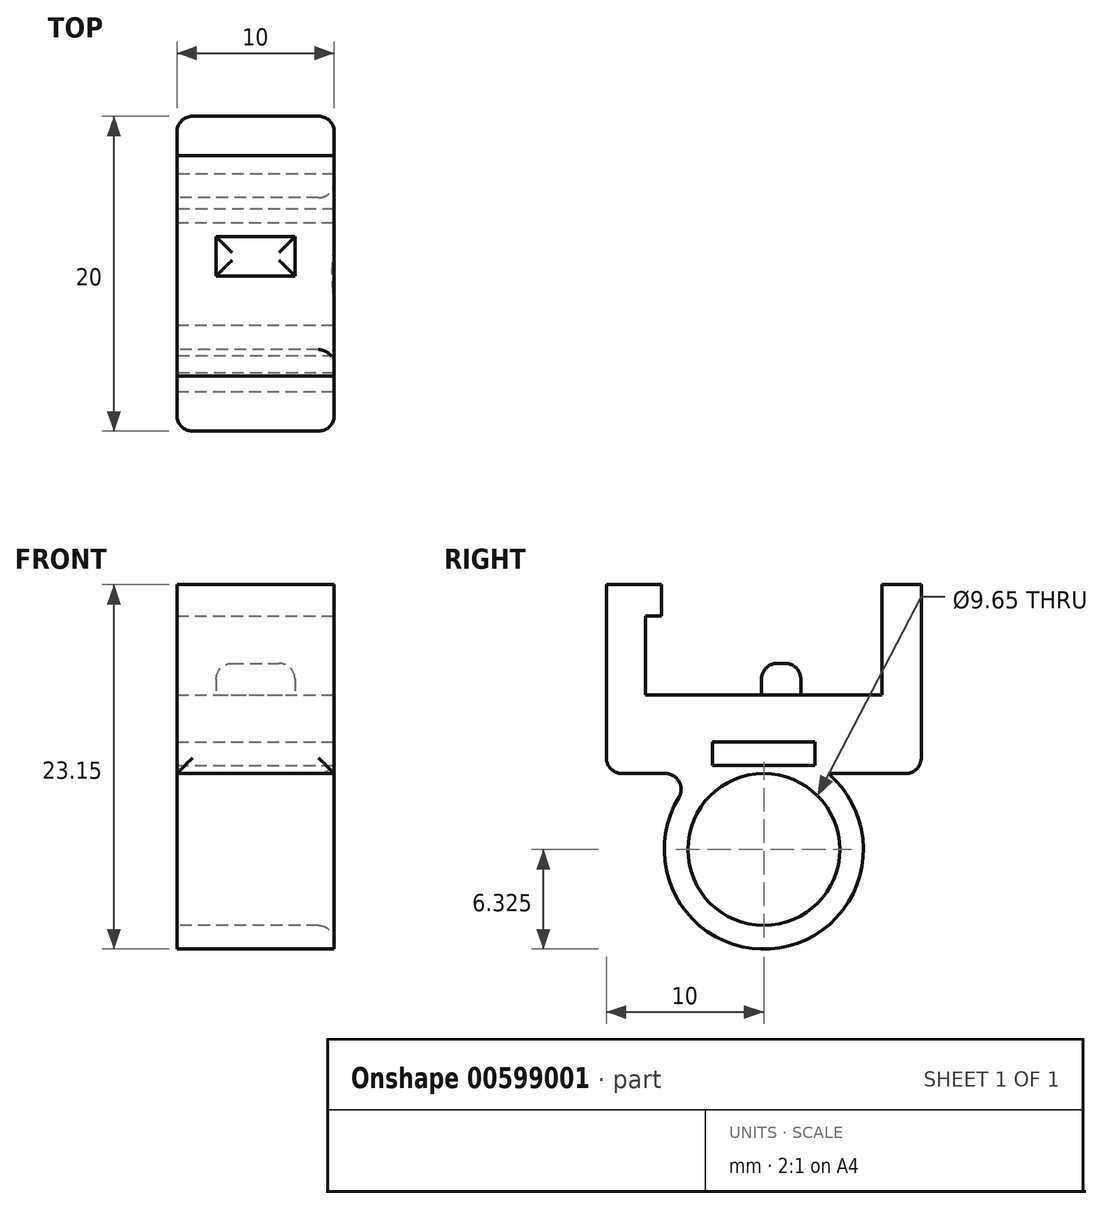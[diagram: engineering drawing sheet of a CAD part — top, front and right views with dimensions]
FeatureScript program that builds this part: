
annotation { "Feature Type Name" : "Feature", "Feature Type Description" : "" }
export const myFeature = defineFeature(function(context is Context, id is Id, definition is map)
    precondition{}
    {
        {
            var Q0;
            Q0=qCreatedBy(makeId("Top.planeOp"),FACE);
            var sketch = newSketch(context, id + "F0", { "sketchPlane" : qUnion([Q0])});
            skLineSegment(sketch, "E0.bottom", {"start": v(5, -10) * mm, "end": v(-5, -10) * mm});
            skLineSegment(sketch, "E0.top", {"start": v(5, 10) * mm, "end": v(-5, 10) * mm});
            skLineSegment(sketch, "E0.left", {"start": v(5, -10) * mm, "end": v(5, 10) * mm});
            skLineSegment(sketch, "E0.right", {"start": v(-5, -10) * mm, "end": v(-5, 10) * mm});
            skPoint(sketch, "E0.middle", {"position": v(0, 0) * mm});
            skSolve(sketch);
        }
        {
            var Q0;
            Q0 = qSketchRegion(id + "F0", true);
            extrude(context, id + "F1", {"entities" : qUnion([Q0]), "depth" : 5 * mm, "offsetDistance" : 25 * mm});
        }
        {
            var Q0;
            Q0=makeQuery(id+"F1.opExtrude","CAP_FACE",FACE,{"disambiguationData":[OSD([sQuery(id+"F0.wireOp",EDGE,"E0.bottom"),sQuery(id+"F0.wireOp",EDGE,"E0.top"),sQuery(id+"F0.wireOp",EDGE,"E0.left"),sQuery(id+"F0.wireOp",EDGE,"E0.right")])],"isStart":false});
            var sketch = newSketch(context, id + "F2", { "sketchPlane" : qUnion([Q0])});
            skLineSegment(sketch, "E1.bottom", {"start": v(-5, -7.5) * mm, "end": v(5, -7.5) * mm});
            skLineSegment(sketch, "E1.top", {"start": v(-5, -10) * mm, "end": v(5, -10) * mm});
            skLineSegment(sketch, "E1.left", {"start": v(-5, -7.5) * mm, "end": v(-5, -10) * mm});
            skLineSegment(sketch, "E1.right", {"start": v(5, -7.5) * mm, "end": v(5, -10) * mm});
            skLineSegment(sketch, "E2.MirrorCS", {"start": v(-5, 7.5) * mm, "end": v(5, 7.5) * mm});
            skLineSegment(sketch, "E3.MirrorCS", {"start": v(-5, 7.5) * mm, "end": v(-5, 10) * mm});
            skLineSegment(sketch, "E4.MirrorCS", {"start": v(-5, 10) * mm, "end": v(5, 10) * mm});
            skLineSegment(sketch, "E5.MirrorCS", {"start": v(5, 7.5) * mm, "end": v(5, 10) * mm});
            skSolve(sketch);
        }
        {
            var Q0;
            Q0 = qSketchRegion(id + "F2", true);
            extrude(context, id + "F3", {"entities" : qUnion([Q0]), "operationType" : NewBodyOperationType.ADD, "depth" : 7 * mm, "offsetDistance" : 25 * mm});
        }
        {
            var Q0;
            Q0=makeQuery(id+"F3.opExtrude","SWEPT_FACE",FACE,{"disambiguationData":[OSD([sQuery(id+"F2.wireOp",EDGE,"E1.bottom")])]});
            var sketch = newSketch(context, id + "F4", { "sketchPlane" : qUnion([Q0])});
            skLineSegment(sketch, "E6.bottom", {"start": v(5, 12) * mm, "end": v(-5, 12) * mm});
            skLineSegment(sketch, "E6.top", {"start": v(5, 10) * mm, "end": v(-5, 10) * mm});
            skLineSegment(sketch, "E6.left", {"start": v(5, 12) * mm, "end": v(5, 10) * mm});
            skLineSegment(sketch, "E6.right", {"start": v(-5, 12) * mm, "end": v(-5, 10) * mm});
            skSolve(sketch);
        }
        {
            var Q0;
            Q0 = qSketchRegion(id + "F4", true);
            extrude(context, id + "F5", {"entities" : qUnion([Q0]), "operationType" : NewBodyOperationType.ADD, "depth" : 1 * mm, "offsetDistance" : 25 * mm});
        }
        {
            var Q0;
            Q0=makeQuery(id+"F1.opExtrude","CAP_FACE",FACE,{"disambiguationData":[OSD([sQuery(id+"F0.wireOp",EDGE,"E0.bottom"),sQuery(id+"F0.wireOp",EDGE,"E0.top"),sQuery(id+"F0.wireOp",EDGE,"E0.left"),sQuery(id+"F0.wireOp",EDGE,"E0.right")])],"isStart":false});
            var sketch = newSketch(context, id + "F6", { "sketchPlane" : qUnion([Q0])});
            skLineSegment(sketch, "E7.bottom", {"start": v(-2.5, 2.35) * mm, "end": v(2.5, 2.35) * mm});
            skLineSegment(sketch, "E7.top", {"start": v(-2.5, -0.15) * mm, "end": v(2.5, -0.15) * mm});
            skLineSegment(sketch, "E7.left", {"start": v(-2.5, 2.35) * mm, "end": v(-2.5, -0.15) * mm});
            skLineSegment(sketch, "E7.right", {"start": v(2.5, 2.35) * mm, "end": v(2.5, -0.15) * mm});
            skSolve(sketch);
        }
        {
            var Q0;
            Q0 = qSketchRegion(id + "F6", true);
            extrude(context, id + "F7", {"entities" : qUnion([Q0]), "operationType" : NewBodyOperationType.ADD, "depth" : 2 * mm, "offsetDistance" : 25 * mm});
        }
        {
            var Q0;
            Q0=makeQuery(id+"F3.opExtrude","CAP_EDGE",EDGE,{"disambiguationData":[OSD([sQuery(id+"F2.wireOp",EDGE,"E2.MirrorCS")])],"isStart":true});
            var Q1;
            Q1=makeQuery(id+"F3.opExtrude","CAP_EDGE",EDGE,{"disambiguationData":[OSD([sQuery(id+"F2.wireOp",EDGE,"E1.bottom")])],"isStart":true});
            var Q2;
            Q2=makeQuery(id+"F1.opExtrude","CAP_EDGE",EDGE,{"disambiguationData":[OSD([sQuery(id+"F0.wireOp",EDGE,"E0.top")])],"isStart":true});
            var Q3;
            Q3=makeQuery(id+"F1.opExtrude","CAP_EDGE",EDGE,{"disambiguationData":[OSD([sQuery(id+"F0.wireOp",EDGE,"E0.bottom")])],"isStart":true});
            var Q4;
            Q4=makeQuery(id+"F3.boolean.opBoolean","MERGE",EDGE,{"derivedFrom":[makeQuery(id+"F1.opExtrude","SWEPT_EDGE",EDGE,{"disambiguationData":[OSD([sQuery(id+"F0.wireOp",EDGE,"E0.bottom"),sQuery(id+"F0.wireOp",EDGE,"E0.left")])]}),makeQuery(id+"F3.opExtrude","SWEPT_EDGE",EDGE,{"disambiguationData":[OSD([sQuery(id+"F2.wireOp",EDGE,"E1.top"),sQuery(id+"F2.wireOp",EDGE,"E1.right")])]})]});
            var Q5;
            Q5=makeQuery(id+"F3.boolean.opBoolean","MERGE",EDGE,{"derivedFrom":[makeQuery(id+"F1.opExtrude","SWEPT_EDGE",EDGE,{"disambiguationData":[OSD([sQuery(id+"F0.wireOp",EDGE,"E0.bottom"),sQuery(id+"F0.wireOp",EDGE,"E0.right")])]}),makeQuery(id+"F3.opExtrude","SWEPT_EDGE",EDGE,{"disambiguationData":[OSD([sQuery(id+"F2.wireOp",EDGE,"E1.top"),sQuery(id+"F2.wireOp",EDGE,"E1.left")])]})]});
            var Q6;
            Q6=makeQuery(id+"F3.boolean.opBoolean","MERGE",EDGE,{"derivedFrom":[makeQuery(id+"F1.opExtrude","SWEPT_EDGE",EDGE,{"disambiguationData":[OSD([sQuery(id+"F0.wireOp",EDGE,"E0.top"),sQuery(id+"F0.wireOp",EDGE,"E0.left")])]}),makeQuery(id+"F3.opExtrude","SWEPT_EDGE",EDGE,{"disambiguationData":[OSD([sQuery(id+"F2.wireOp",EDGE,"E4.MirrorCS"),sQuery(id+"F2.wireOp",EDGE,"E5.MirrorCS")])]})]});
            var Q7;
            Q7=makeQuery(id+"F3.boolean.opBoolean","MERGE",EDGE,{"derivedFrom":[makeQuery(id+"F1.opExtrude","SWEPT_EDGE",EDGE,{"disambiguationData":[OSD([sQuery(id+"F0.wireOp",EDGE,"E0.top"),sQuery(id+"F0.wireOp",EDGE,"E0.right")])]}),makeQuery(id+"F3.opExtrude","SWEPT_EDGE",EDGE,{"disambiguationData":[OSD([sQuery(id+"F2.wireOp",EDGE,"E3.MirrorCS"),sQuery(id+"F2.wireOp",EDGE,"E4.MirrorCS")])]})]});
            var Q8;
            Q8=makeQuery(id+"F7.opExtrude","CAP_FACE",FACE,{"disambiguationData":[OSD([sQuery(id+"F6.wireOp",EDGE,"E7.bottom"),sQuery(id+"F6.wireOp",EDGE,"E7.top"),sQuery(id+"F6.wireOp",EDGE,"E7.left"),sQuery(id+"F6.wireOp",EDGE,"E7.right")])],"isStart":false});
            fillet(context, id + "F8", {"entities" : qUnion([Q0, Q1, Q2, Q3, Q4, Q5, Q6, Q7, Q8]), "radius" : 1 * mm, "tangentPropagation" : true, "allowEdgeOverflow" : false});
        }
        {
            var Q0;
            Q0=makeQuery(id+"F5.boolean.opBoolean","MERGE",FACE,{"derivedFrom":[makeQuery(id+"F3.boolean.opBoolean","MERGE",FACE,{"derivedFrom":[makeQuery(id+"F1.opExtrude","SWEPT_FACE",FACE,{"disambiguationData":[OSD([sQuery(id+"F0.wireOp",EDGE,"E0.left")])]}),makeQuery(id+"F3.opExtrude","SWEPT_FACE",FACE,{"disambiguationData":[OSD([sQuery(id+"F2.wireOp",EDGE,"E1.right")])]}),makeQuery(id+"F3.opExtrude","SWEPT_FACE",FACE,{"disambiguationData":[OSD([sQuery(id+"F2.wireOp",EDGE,"E5.MirrorCS")])]})]}),makeQuery(id+"F5.opExtrude","SWEPT_FACE",FACE,{"disambiguationData":[OSD([sQuery(id+"F4.wireOp",EDGE,"E6.right")])]})]});
            var sketch = newSketch(context, id + "F9", { "sketchPlane" : qUnion([Q0])});
            skLineSegment(sketch, "E8.bottom", {"start": v(-3.25, 2) * mm, "end": v(3.25, 2) * mm});
            skLineSegment(sketch, "E8.top", {"start": v(-3.25, 0.5) * mm, "end": v(3.25, 0.5) * mm});
            skLineSegment(sketch, "E8.left", {"start": v(-3.25, 2) * mm, "end": v(-3.25, 0.5) * mm});
            skLineSegment(sketch, "E8.right", {"start": v(3.25, 2) * mm, "end": v(3.25, 0.5) * mm});
            skSolve(sketch);
        }
        {
            var Q0;
            Q0 = qSketchRegion(id + "F9", true);
            extrude(context, id + "F10", {"entities" : qUnion([Q0]), "operationType" : NewBodyOperationType.REMOVE, "endBound" : BoundingType.THROUGH_ALL, "oppositeDirection" : true, "depth" : 25 * mm, "offsetDistance" : 25 * mm});
        }
        {
            var Q0;
            Q0=qCreatedBy(makeId("Right.planeOp"),FACE);
            var sketch = newSketch(context, id + "F11", { "sketchPlane" : qUnion([Q0])});
            skCircle(sketch, "E9", {"center": v(0, -4.83) * mm, "radius": 4.83 * mm});
            skArc(sketch, "E10", {"start": v(-4.09, 0) * mm, "mid": v(0, -11.15) * mm, "end": v(4.09, 0) * mm});
            skLineSegment(sketch, "E11", {"start": v(4.09, 0) * mm, "end": v(-4.09, 0) * mm});
            skSolve(sketch);
        }
        {
            var Q0;
            Q0 = qSketchRegion(id + "F11", true);
            extrude(context, id + "F12", {"entities" : qUnion([Q0]), "operationType" : NewBodyOperationType.ADD, "endBound" : BoundingType.SYMMETRIC, "depth" : 10 * mm, "offsetDistance" : 25 * mm});
        }
        {
            var Q0;
            Q0=makeQuery(id+"F12.boolean.opBoolean","MERGE",FACE,{"derivedFrom":[makeQuery(id+"F5.boolean.opBoolean","MERGE",FACE,{"derivedFrom":[makeQuery(id+"F3.boolean.opBoolean","MERGE",FACE,{"derivedFrom":[makeQuery(id+"F1.opExtrude","SWEPT_FACE",FACE,{"disambiguationData":[OSD([sQuery(id+"F0.wireOp",EDGE,"E0.right")])]}),makeQuery(id+"F3.opExtrude","SWEPT_FACE",FACE,{"disambiguationData":[OSD([sQuery(id+"F2.wireOp",EDGE,"E1.left")])]}),makeQuery(id+"F3.opExtrude","SWEPT_FACE",FACE,{"disambiguationData":[OSD([sQuery(id+"F2.wireOp",EDGE,"E3.MirrorCS")])]})]}),makeQuery(id+"F5.opExtrude","SWEPT_FACE",FACE,{"disambiguationData":[OSD([sQuery(id+"F4.wireOp",EDGE,"E6.left")])]})]}),makeQuery(id+"F12.opExtrude","CAP_FACE",FACE,{"disambiguationData":[OSD([sQuery(id+"F11.wireOp",EDGE,"E10"),sQuery(id+"F11.wireOp",EDGE,"E11")])],"isStart":true})]});
            var sketch = newSketch(context, id + "F13", { "sketchPlane" : qUnion([Q0])});
            skCircle(sketch, "E12", {"center": v(0, -4.83) * mm, "radius": 4.83 * mm});
            skSolve(sketch);
        }
        {
            var Q0;
            Q0 = qSketchRegion(id + "F13", true);
            extrude(context, id + "F14", {"entities" : qUnion([Q0]), "operationType" : NewBodyOperationType.REMOVE, "endBound" : BoundingType.THROUGH_ALL, "oppositeDirection" : true, "depth" : 25 * mm, "offsetDistance" : 25 * mm});
        }
        {
            var Q0;
            {var subQ0=sQuery(id+"F11.wireOp",EDGE,"E11");var subQ1=sQuery(id+"F11.wireOp",EDGE,"E10");Q0=makeQuery(id+"F12.opExtrude","SWEPT_EDGE",EDGE,{"disambiguationData":[OSD([subQ1,subQ0]),TDD([makeQuery(id+"F11.imprint","INTERSECT",VERTEX,{"disambiguationData":[OD(1.0)],"derivedFrom":[subQ1,subQ0]})])]});}
            var Q1;
            {var subQ0=sQuery(id+"F11.wireOp",EDGE,"E11");var subQ1=sQuery(id+"F11.wireOp",EDGE,"E10");Q1=makeQuery(id+"F12.opExtrude","SWEPT_EDGE",EDGE,{"disambiguationData":[OSD([subQ1,subQ0]),TDD([makeQuery(id+"F11.imprint","INTERSECT",VERTEX,{"disambiguationData":[OD(0.0)],"derivedFrom":[subQ1,subQ0]})])]});}
            var Q2;
            Q2=makeQuery(id+"F14.boolean.opBoolean","COPY",EDGE,{"derivedFrom":makeQuery(id+"F14.opExtrude","CAP_EDGE",EDGE,{"disambiguationData":[OSD([sQuery(id+"F13.wireOp",EDGE,"E12")])],"isStart":true})});
            var Q3;
            Q3=makeQuery(id+"F14.boolean.opBoolean","INTERSECT",EDGE,{"derivedFrom":[makeQuery(id+"F12.boolean.opBoolean","MERGE",FACE,{"derivedFrom":[makeQuery(id+"F5.boolean.opBoolean","MERGE",FACE,{"derivedFrom":[makeQuery(id+"F3.boolean.opBoolean","MERGE",FACE,{"derivedFrom":[makeQuery(id+"F1.opExtrude","SWEPT_FACE",FACE,{"disambiguationData":[OSD([sQuery(id+"F0.wireOp",EDGE,"E0.left")])]}),makeQuery(id+"F3.opExtrude","SWEPT_FACE",FACE,{"disambiguationData":[OSD([sQuery(id+"F2.wireOp",EDGE,"E1.right")])]}),makeQuery(id+"F3.opExtrude","SWEPT_FACE",FACE,{"disambiguationData":[OSD([sQuery(id+"F2.wireOp",EDGE,"E5.MirrorCS")])]})]}),makeQuery(id+"F5.opExtrude","SWEPT_FACE",FACE,{"disambiguationData":[OSD([sQuery(id+"F4.wireOp",EDGE,"E6.right")])]})]}),makeQuery(id+"F12.opExtrude","CAP_FACE",FACE,{"disambiguationData":[OSD([sQuery(id+"F11.wireOp",EDGE,"E10"),sQuery(id+"F11.wireOp",EDGE,"E11")])],"isStart":false})]}),makeQuery(id+"F14.opExtrude","SWEPT_FACE",FACE,{"disambiguationData":[OSD([sQuery(id+"F13.wireOp",EDGE,"E12")])]})]});
            fillet(context, id + "F15", {"entities" : qUnion([Q0, Q1, Q2, Q3]), "radius" : 1 * mm, "tangentPropagation" : true, "allowEdgeOverflow" : false});
        }
    });
